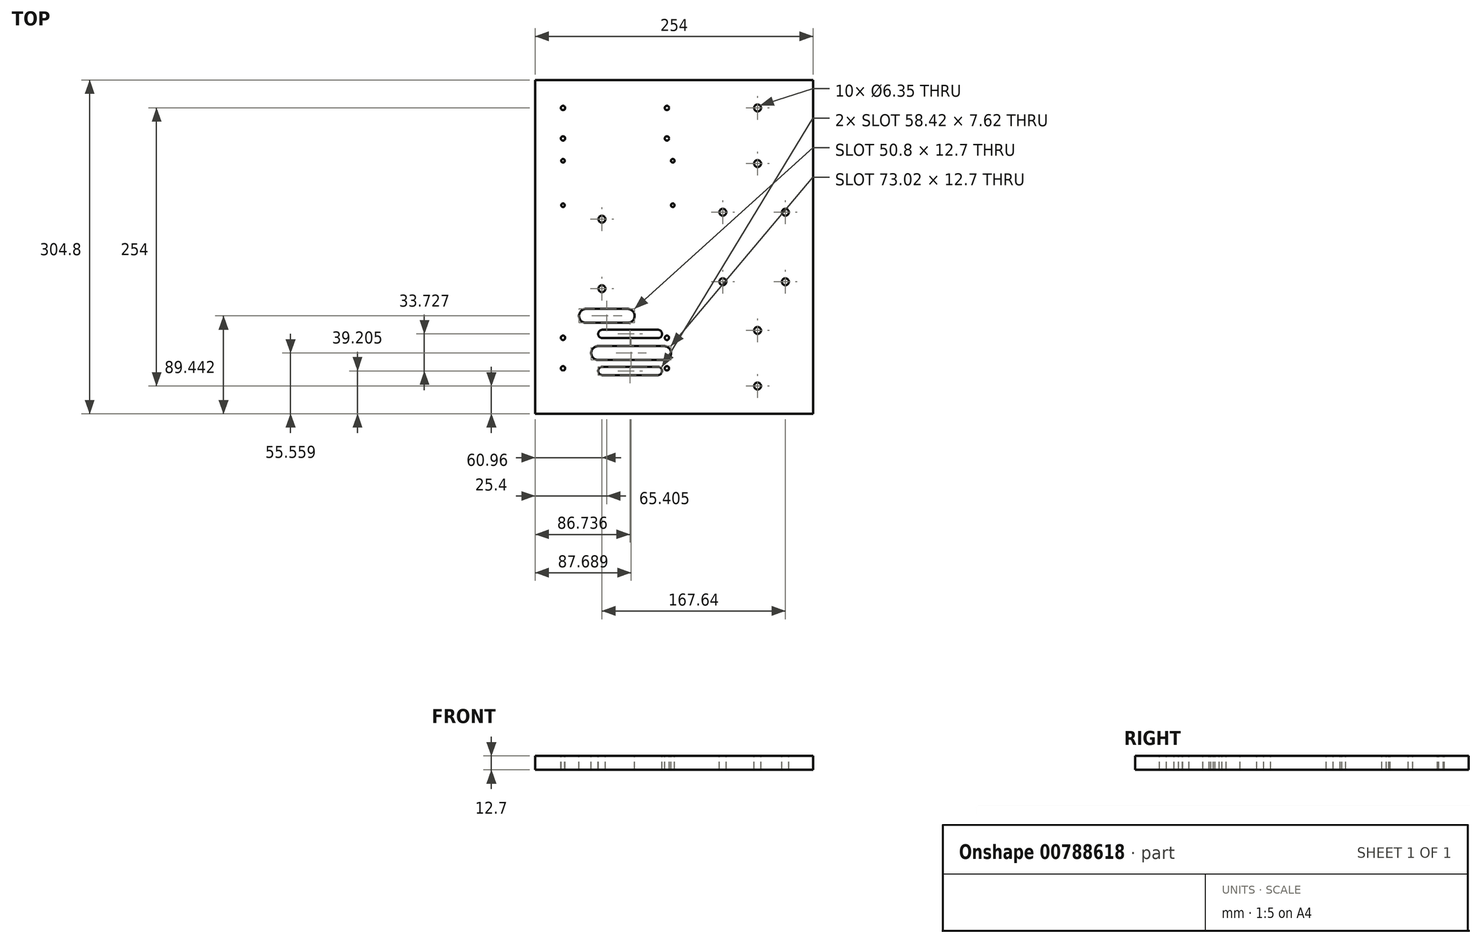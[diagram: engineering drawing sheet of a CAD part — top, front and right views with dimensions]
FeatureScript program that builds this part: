
annotation { "Feature Type Name" : "Feature", "Feature Type Description" : "" }
export const myFeature = defineFeature(function(context is Context, id is Id, definition is map)
    precondition{}
    {
        {
            var Q0;
            Q0=qCreatedBy(makeId("Top.planeOp"),FACE);
            var sketch = newSketch(context, id + "F0", { "sketchPlane" : qUnion([Q0])});
            skLineSegment(sketch, "E0.bottom", {"start": v(127, 152.4) * mm, "end": v(-127, 152.4) * mm});
            skLineSegment(sketch, "E0.top", {"start": v(127, -152.4) * mm, "end": v(-127, -152.4) * mm});
            skLineSegment(sketch, "E0.left", {"start": v(127, 152.4) * mm, "end": v(127, -152.4) * mm});
            skLineSegment(sketch, "E0.right", {"start": v(-127, 152.4) * mm, "end": v(-127, -152.4) * mm});
            skPoint(sketch, "E0.middle", {"position": v(0, 0) * mm});
            skSolve(sketch);
        }
        {
            var Q0;
            Q0=makeQuery(id+"F0.imprint","IMPRINT",FACE,{"disambiguationData":[TD([[makeQuery(id+"F0.imprint","IMPRINT",EDGE,{"derivedFrom":sQuery(id+"F0.wireOp",EDGE,"E0.bottom")}),1.0]])]});
            extrude(context, id + "F1", {"entities" : qUnion([Q0]), "depth" : 12.7 * mm, "offsetDistance" : 25.4 * mm});
        }
        {
            var Q0;
            Q0=makeQuery(id+"F1.opExtrude","CAP_FACE",FACE,{"disambiguationData":[OSD([sQuery(id+"F0.wireOp",EDGE,"E0.bottom"),sQuery(id+"F0.wireOp",EDGE,"E0.top"),sQuery(id+"F0.wireOp",EDGE,"E0.left"),sQuery(id+"F0.wireOp",EDGE,"E0.right")])],"isStart":false});
            var sketch = newSketch(context, id + "F2", { "sketchPlane" : qUnion([Q0])});
            skCircle(sketch, "E1", {"center": v(-101.6, 127) * mm, "radius": 1.98 * mm});
            skCircle(sketch, "E2", {"center": v(-101.6, 99.11) * mm, "radius": 1.98 * mm});
            skCircle(sketch, "E3", {"center": v(-6.6, 127) * mm, "radius": 1.98 * mm});
            skCircle(sketch, "E4", {"center": v(-6.6, 99.11) * mm, "radius": 1.98 * mm});
            skCircle(sketch, "E5", {"center": v(-101.6, -82.97) * mm, "radius": 1.98 * mm});
            skCircle(sketch, "E6", {"center": v(-6.6, -82.97) * mm, "radius": 1.98 * mm});
            skCircle(sketch, "E7", {"center": v(-6.6, -110.86) * mm, "radius": 1.98 * mm});
            skCircle(sketch, "E8", {"center": v(-101.6, -110.86) * mm, "radius": 1.98 * mm});
            skCircle(sketch, "E9", {"center": v(-101.6, 78.74) * mm, "radius": 1.65 * mm});
            skCircle(sketch, "E10", {"center": v(-101.6, 38.12) * mm, "radius": 1.65 * mm});
            skCircle(sketch, "E11", {"center": v(-66.04, 25.4) * mm, "radius": 3.18 * mm});
            skCircle(sketch, "E12", {"center": v(-66.04, -38.1) * mm, "radius": 3.18 * mm});
            skCircle(sketch, "E13", {"center": v(76.2, -76.2) * mm, "radius": 3.18 * mm});
            skCircle(sketch, "E14", {"center": v(76.2, -127) * mm, "radius": 3.18 * mm});
            skCircle(sketch, "E15", {"center": v(76.2, 127) * mm, "radius": 3.18 * mm});
            skCircle(sketch, "E16", {"center": v(76.2, 76.2) * mm, "radius": 3.18 * mm});
            skCircle(sketch, "E17", {"center": v(44.45, 31.75) * mm, "radius": 3.18 * mm});
            skCircle(sketch, "E18", {"center": v(101.6, 31.75) * mm, "radius": 3.18 * mm});
            skCircle(sketch, "E19", {"center": v(44.45, -31.75) * mm, "radius": 3.18 * mm});
            skCircle(sketch, "E20", {"center": v(101.6, -31.75) * mm, "radius": 3.18 * mm});
            skLineSegment(sketch, "E21.bottom", {"start": v(-69.47, -90.5) * mm, "end": v(-9.15, -90.5) * mm});
            skLineSegment(sketch, "E21.top", {"start": v(-69.47, -103.2) * mm, "end": v(-9.15, -103.2) * mm});
            skLineSegment(sketch, "E21.left", {"start": v(-69.47, -90.5) * mm, "end": v(-69.47, -103.2) * mm});
            skLineSegment(sketch, "E21.right", {"start": v(-9.15, -90.5) * mm, "end": v(-9.15, -103.2) * mm});
            skLineSegment(sketch, "E22.bottom", {"start": v(-65.66, -109.39) * mm, "end": v(-14.86, -109.39) * mm});
            skLineSegment(sketch, "E22.top", {"start": v(-65.66, -117) * mm, "end": v(-14.86, -117) * mm});
            skLineSegment(sketch, "E22.left", {"start": v(-65.66, -109.39) * mm, "end": v(-65.66, -117) * mm});
            skLineSegment(sketch, "E22.right", {"start": v(-14.86, -109.39) * mm, "end": v(-14.86, -117) * mm});
            skLineSegment(sketch, "E23.bottom", {"start": v(-80.64, -56.6) * mm, "end": v(-42.54, -56.6) * mm});
            skLineSegment(sketch, "E23.top", {"start": v(-80.64, -69.3) * mm, "end": v(-42.54, -69.3) * mm});
            skLineSegment(sketch, "E23.left", {"start": v(-80.64, -56.6) * mm, "end": v(-80.64, -69.3) * mm});
            skLineSegment(sketch, "E23.right", {"start": v(-42.54, -56.6) * mm, "end": v(-42.54, -69.3) * mm});
            skLineSegment(sketch, "E24.bottom", {"start": v(-65.66, -75.66) * mm, "end": v(-14.86, -75.66) * mm});
            skLineSegment(sketch, "E24.top", {"start": v(-65.66, -83.28) * mm, "end": v(-14.86, -83.28) * mm});
            skLineSegment(sketch, "E24.left", {"start": v(-65.66, -75.66) * mm, "end": v(-65.66, -83.28) * mm});
            skLineSegment(sketch, "E24.right", {"start": v(-14.86, -75.66) * mm, "end": v(-14.86, -83.28) * mm});
            skLineSegment(sketch, "E25", {"start": v(-69.47, -103.2) * mm, "end": v(-69.47, -96.84) * mm});
            skCircle(sketch, "E26", {"center": v(-1.29, 78.74) * mm, "radius": 1.65 * mm});
            skCircle(sketch, "E27", {"center": v(-1.29, 38.12) * mm, "radius": 1.65 * mm});
            skArc(sketch, "E28", {"start": v(-69.47, -90.5) * mm, "mid": v(-75.82, -96.84) * mm, "end": v(-69.47, -103.2) * mm});
            skArc(sketch, "E29", {"start": v(-9.15, -103.2) * mm, "mid": v(-2.8, -96.84) * mm, "end": v(-9.15, -90.5) * mm});
            skArc(sketch, "E30", {"start": v(-65.66, -75.66) * mm, "mid": v(-69.47, -79.47) * mm, "end": v(-65.66, -83.28) * mm});
            skArc(sketch, "E31", {"start": v(-14.86, -83.28) * mm, "mid": v(-11.05, -79.47) * mm, "end": v(-14.86, -75.66) * mm});
            skArc(sketch, "E32", {"start": v(-14.86, -117) * mm, "mid": v(-11.05, -113.2) * mm, "end": v(-14.86, -109.39) * mm});
            skArc(sketch, "E33", {"start": v(-65.66, -109.39) * mm, "mid": v(-69.47, -113.2) * mm, "end": v(-65.66, -117) * mm});
            skArc(sketch, "E34", {"start": v(-42.54, -69.3) * mm, "mid": v(-36.2, -62.96) * mm, "end": v(-42.54, -56.6) * mm});
            skArc(sketch, "E35", {"start": v(-80.64, -56.6) * mm, "mid": v(-87, -62.96) * mm, "end": v(-80.64, -69.3) * mm});
            skSolve(sketch);
        }
        {
            var Q0;
            Q0=qSketchRegion(id+"F2",true);
            extrude(context, id + "F3", {"entities" : qUnion([Q0]), "operationType" : NewBodyOperationType.REMOVE, "oppositeDirection" : true, "depth" : 25.4 * mm, "offsetDistance" : 25.4 * mm});
        }
    });
